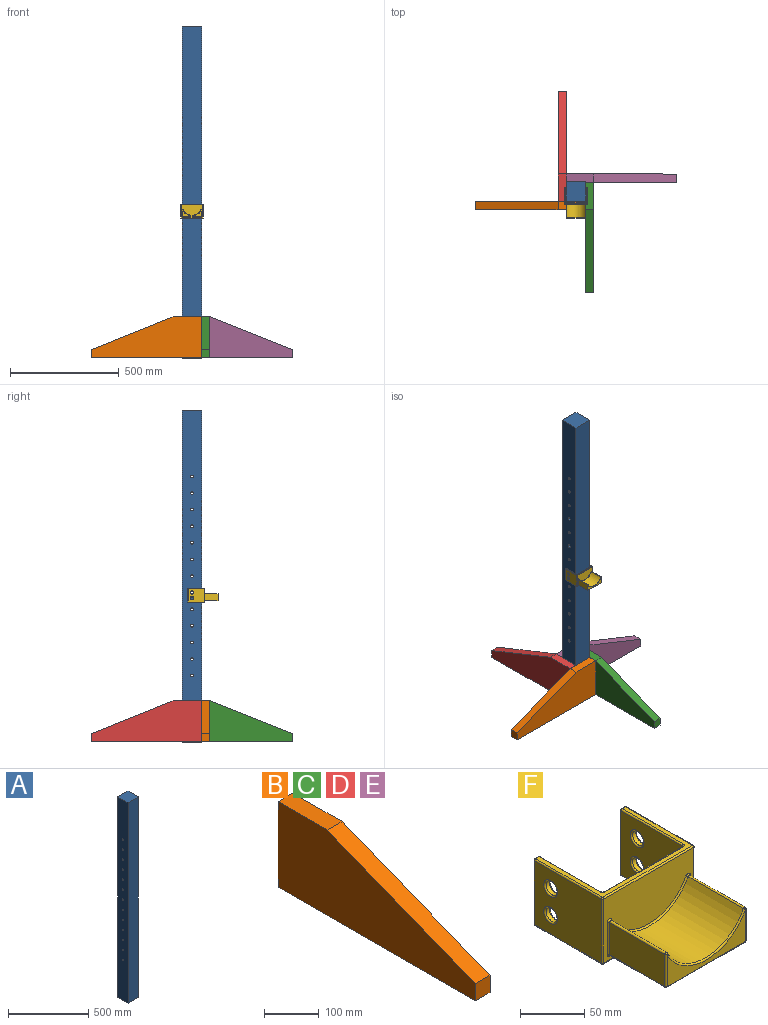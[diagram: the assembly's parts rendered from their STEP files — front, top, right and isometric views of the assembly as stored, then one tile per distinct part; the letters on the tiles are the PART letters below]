
ASSEMBLY  parts=6 mates=5
PART A: 19 faces, bbox 88.9x88.9x1524 mm
  f0: plane 1524x88.9mm, normal (0,1,0), area 135483.6mm2, adj f1,f3,f4,f5
  f1: plane 1524x88.9mm, normal (-1,0,0), area 133836.8mm2, adj f0,f2,f4,f5,f6,f7,f8,f9
  f2: plane 1524x88.9mm, normal (0,-1,0), area 135483.6mm2, adj f1,f3,f4,f5
  f3: plane 1524x88.9mm, normal (1,0,0), area 133836.8mm2, adj f0,f2,f4,f5,f6,f7,f8,f9
  f4: plane 88.9x88.9mm, normal (0,0,1), area 7903.2mm2, adj f0,f1,f2,f3
  f5: plane 88.9x88.9mm, normal (0,0,-1), area 7903.2mm2, adj f0,f1,f2,f3
  f6: cylinder r=6.35mm len=88.9mm, axis (1,0,0), area 3547mm2, adj f1,f3
  f7: cylinder r=6.35mm len=88.9mm, axis (1,0,0), area 3547mm2, adj f1,f3
  f8: cylinder r=6.35mm len=88.9mm, axis (1,0,0), area 3547mm2, adj f1,f3
  f9: cylinder r=6.35mm len=88.9mm, axis (1,0,0), area 3547mm2, adj f1,f3
  f10: cylinder r=6.35mm len=88.9mm, axis (1,0,0), area 3547mm2, adj f1,f3
  f11: cylinder r=6.35mm len=88.9mm, axis (1,0,0), area 3547mm2, adj f1,f3
  f12: cylinder r=6.35mm len=88.9mm, axis (1,0,0), area 3547mm2, adj f1,f3
  f13: cylinder r=6.35mm len=88.9mm, axis (1,0,0), area 3547mm2, adj f1,f3
  f14: cylinder r=6.35mm len=88.9mm, axis (1,0,0), area 3547mm2, adj f1,f3
  f15: cylinder r=6.35mm len=88.9mm, axis (1,0,0), area 3547mm2, adj f1,f3
  f16: cylinder r=6.35mm len=88.9mm, axis (1,0,0), area 3547mm2, adj f1,f3
  f17: cylinder r=6.35mm len=88.9mm, axis (1,0,0), area 3547mm2, adj f1,f3
  f18: cylinder r=6.35mm len=88.9mm, axis (1,0,0), area 3547mm2, adj f1,f3
PART B: 7 faces, bbox 38.1x508x190.5 mm
  f0: plane 127x38.1mm, normal (0,0,1), area 4838.7mm2, adj f1,f4,f5,f6
  f1: plane 381x152.4mm, normal (0,-0.37,0.93), area 15634.3mm2, adj f0,f2,f5,f6
  f2: plane 38.1x38.1mm, normal (0,-1,0), area 1451.6mm2, adj f1,f3,f5,f6
  f3: plane 508x38.1mm, normal (0,0,-1), area 19354.8mm2, adj f2,f4,f5,f6
  f4: plane 190.5x38.1mm, normal (0,1,0), area 7258.1mm2, adj f0,f3,f5,f6
  f5: plane 508x190.5mm, normal (1,0,0), area 67741.8mm2, adj f0,f1,f2,f3,f4
  f6: plane 508x190.5mm, normal (-1,0,0), area 67741.8mm2, adj f0,f1,f2,f3,f4
PART C: same geometry as B
PART D: same geometry as B
PART E: same geometry as B
PART F: 87 faces, bbox 101.6x139.7x63.5 mm
  f0: plane 99.06x73.66mm, normal (0,0,-1), area 912.4mm2, adj f35,f39,f40,f44,f49,f50,f54,f59
  f1: plane 99.06x73.66mm, normal (0,0,1), area 912.4mm2, adj f42,f47,f52,f53,f57,f63,f64,f68
  f2: plane 60.96x3.81mm, normal (0,1,0), area 232.3mm2, adj f35,f38,f41,f42
  f3: plane 73.66x60.96mm, normal (-1,0,0), area 4125.5mm2, adj f40,f41,f51,f52,f85,f86
  f4: plane 99.06x60.96mm, normal (0,-1,0), area 4386.5mm2, adj f20,f25,f26,f29,f30,f32,f33,f34
  f5: plane 73.66x60.96mm, normal (1,0,0), area 4125.5mm2, adj f61,f62,f70,f71,f79,f82
  f6: plane 60.96x3.81mm, normal (0,1,0), area 232.3mm2, adj f60,f69,f70,f74
  f7: plane 67.31x60.96mm, normal (1,0,0), area 3738.4mm2, adj f38,f39,f47,f48,f80,f83
  f8: plane 86.36x60.96mm, normal (0,1,0), area 5264.5mm2, adj f48,f49,f57,f58
  f9: plane 67.31x60.96mm, normal (-1,0,0), area 3738.4mm2, adj f58,f59,f68,f69,f81,f84
  f10: cylinder r=46.99mm len=84.09mm, axis (0,1,0), area 6346.8mm2, adj f23,f28,f31,f34
  f11: plane 60.96x30.52mm, normal (-1,0,0), area 1860.3mm2, adj f18,f19,f28,f29
  f12: plane 86.36x60.96mm, normal (0,0,-1), area 5264.5mm2, adj f15,f19,f20,f21
  f13: plane 60.96x30.52mm, normal (1,0,0), area 1860.3mm2, adj f21,f22,f30,f31
  f14: plane 86.36x30.52mm, normal (0,-1,0), area 985.9mm2, adj f15,f18,f22,f23
  f15: cylinder r=1.27mm len=86.36mm, axis (-1,0,0), area 172.3mm2, adj f12,f14,f16,f17
  f16: sphere r=1.27mm, area 2.5mm2, adj f15,f18,f19
  f17: sphere r=1.27mm, area 2.5mm2, adj f15,f21,f22
  f18: cylinder r=1.27mm len=30.52mm, axis (0,0,1), area 60.9mm2, adj f11,f14,f16,f24
  f19: cylinder r=1.27mm len=60.96mm, axis (0,1,0), area 121.6mm2, adj f11,f12,f16,f25
  f20: cylinder r=1.27mm len=86.36mm, axis (-1,0,0), area 172.3mm2, adj f4,f12,f25,f26
  f21: cylinder r=1.27mm len=60.96mm, axis (0,-1,0), area 121.6mm2, adj f12,f13,f17,f26
  f22: cylinder r=1.27mm len=30.52mm, axis (0,0,-1), area 60.9mm2, adj f13,f14,f17,f27
  f23: torus R=48.26mm, axis (0,-1,0), area 209.7mm2, adj f10,f14,f24,f27
  f24: sphere r=1.27mm, area 4.3mm2, adj f18,f23,f28
  f25: torus R=2.54mm, axis (0,1,0), area 5.4mm2, adj f4,f19,f20,f29
  f26: torus R=2.54mm, axis (0,1,0), area 5.4mm2, adj f4,f20,f21,f30
  f27: sphere r=1.27mm, area 4.3mm2, adj f22,f23,f31
  f28: cylinder r=1.27mm len=60.96mm, axis (0,1,0), area 207.4mm2, adj f10,f11,f24,f32
  f29: cylinder r=1.27mm len=30.52mm, axis (0,0,1), area 60.9mm2, adj f4,f11,f25,f32
  f30: cylinder r=1.27mm len=30.52mm, axis (0,0,-1), area 60.9mm2, adj f4,f13,f26,f33
  f31: cylinder r=1.27mm len=60.96mm, axis (0,1,0), area 207.4mm2, adj f10,f13,f27,f33
  f32: torus R=2.54mm, axis (0,1,0), area 9.3mm2, adj f4,f28,f29,f34
  f33: torus R=2.54mm, axis (0,1,0), area 9.3mm2, adj f4,f30,f31,f34
  f34: torus R=45.72mm, axis (0,1,0), area 205.7mm2, adj f4,f10,f32,f33
  f35: cylinder r=1.27mm len=3.81mm, axis (-1,0,0), area 7.6mm2, adj f0,f2,f36,f37
  f36: sphere r=1.27mm, area 2.5mm2, adj f35,f38,f39
  f37: sphere r=1.27mm, area 2.5mm2, adj f35,f40,f41
  f38: cylinder r=1.27mm len=60.96mm, axis (0,0,1), area 121.6mm2, adj f2,f7,f36,f43
  f39: cylinder r=1.27mm len=67.31mm, axis (0,1,0), area 134.3mm2, adj f0,f7,f36,f44
  f40: cylinder r=1.27mm len=73.66mm, axis (0,-1,0), area 146.9mm2, adj f0,f3,f37,f45
  f41: cylinder r=1.27mm len=60.96mm, axis (0,0,-1), area 121.6mm2, adj f2,f3,f37,f46
  f42: cylinder r=1.27mm len=3.81mm, axis (1,0,0), area 7.6mm2, adj f1,f2,f43,f46
  f43: sphere r=1.27mm, area 2.5mm2, adj f38,f42,f47
  f44: torus R=2.54mm, axis (0,0,1), area 5.4mm2, adj f0,f39,f48,f49
  f45: sphere r=1.27mm, area 2.5mm2, adj f40,f50,f51
  f46: sphere r=1.27mm, area 2.5mm2, adj f41,f42,f52
  f47: cylinder r=1.27mm len=67.31mm, axis (0,-1,0), area 134.3mm2, adj f1,f7,f43,f53
  f48: cylinder r=1.27mm len=60.96mm, axis (0,0,-1), area 121.6mm2, adj f7,f8,f44,f53
  f49: cylinder r=1.27mm len=86.36mm, axis (-1,0,0), area 172.3mm2, adj f0,f8,f44,f54
  f50: cylinder r=1.27mm len=99.06mm, axis (1,0,0), area 197.6mm2, adj f0,f4,f45,f55
  f51: cylinder r=1.27mm len=60.96mm, axis (0,0,1), area 121.6mm2, adj f3,f4,f45,f56
  f52: cylinder r=1.27mm len=73.66mm, axis (0,1,0), area 146.9mm2, adj f1,f3,f46,f56
  f53: torus R=2.54mm, axis (0,0,1), area 5.4mm2, adj f1,f47,f48,f57
  f54: torus R=2.54mm, axis (0,0,1), area 5.4mm2, adj f0,f49,f58,f59
  f55: sphere r=1.27mm, area 2.5mm2, adj f50,f61,f62
  f56: sphere r=1.27mm, area 2.5mm2, adj f51,f52,f63
  f57: cylinder r=1.27mm len=86.36mm, axis (1,0,0), area 172.3mm2, adj f1,f8,f53,f64
  f58: cylinder r=1.27mm len=60.96mm, axis (0,0,1), area 121.6mm2, adj f8,f9,f54,f64
  f59: cylinder r=1.27mm len=67.31mm, axis (0,-1,0), area 134.3mm2, adj f0,f9,f54,f65
  f60: cylinder r=1.27mm len=3.81mm, axis (-1,0,0), area 7.6mm2, adj f0,f6,f65,f66
  f61: cylinder r=1.27mm len=73.66mm, axis (0,1,0), area 146.9mm2, adj f0,f5,f55,f66
  f62: cylinder r=1.27mm len=60.96mm, axis (0,0,-1), area 121.6mm2, adj f4,f5,f55,f67
  f63: cylinder r=1.27mm len=99.06mm, axis (-1,0,0), area 197.6mm2, adj f1,f4,f56,f67
  f64: torus R=2.54mm, axis (0,0,1), area 5.4mm2, adj f1,f57,f58,f68
  f65: sphere r=1.27mm, area 2.5mm2, adj f59,f60,f69
  f66: sphere r=1.27mm, area 2.5mm2, adj f60,f61,f70
  f67: sphere r=1.27mm, area 2.5mm2, adj f62,f63,f71
  f68: cylinder r=1.27mm len=67.31mm, axis (0,1,0), area 134.3mm2, adj f1,f9,f64,f72
  f69: cylinder r=1.27mm len=60.96mm, axis (0,0,-1), area 121.6mm2, adj f6,f9,f65,f72
  f70: cylinder r=1.27mm len=60.96mm, axis (0,0,1), area 121.6mm2, adj f5,f6,f66,f73
  f71: cylinder r=1.27mm len=73.66mm, axis (0,-1,0), area 146.9mm2, adj f1,f5,f67,f73
  f72: sphere r=1.27mm, area 2.5mm2, adj f68,f69,f74
  f73: sphere r=1.27mm, area 2.5mm2, adj f70,f71,f74
  f74: cylinder r=1.27mm len=3.81mm, axis (1,0,0), area 7.6mm2, adj f1,f6,f72,f73
  f75: cylinder r=6.35mm len=12.7mm, axis (-1,0,0), area 152mm2, adj f82,f84
  f76: cylinder r=6.35mm len=12.7mm, axis (-1,0,0), area 152mm2, adj f79,f81
  f77: cylinder r=6.35mm len=12.7mm, axis (-1,0,0), area 152mm2, adj f83,f85
  f78: cylinder r=6.35mm len=12.7mm, axis (-1,0,0), area 152mm2, adj f80,f86
  f79: torus R=7.62mm, axis (-1,0,0), area 85.4mm2, adj f5,f76
  f80: torus R=7.62mm, axis (-1,0,0), area 85.4mm2, adj f7,f78
  f81: torus R=7.62mm, axis (-1,0,0), area 85.4mm2, adj f9,f76
  f82: torus R=7.62mm, axis (-1,0,0), area 85.4mm2, adj f5,f75
  f83: torus R=7.62mm, axis (-1,0,0), area 85.4mm2, adj f7,f77
  f84: torus R=7.62mm, axis (-1,0,0), area 85.4mm2, adj f9,f75
  f85: torus R=7.62mm, axis (-1,0,0), area 85.4mm2, adj f3,f77
  f86: torus R=7.62mm, axis (-1,0,0), area 85.4mm2, adj f3,f78
PLACE A t=(-558.86,284.42,-21.93)mm fixed
PLACE B rot(axis=(0,0,-1),90deg) t=(-476.5,-62.6,300.67)mm
PLACE C t=(-117.26,-332.95,300.67)mm
PLACE D rot(axis=(0,0,-1),180deg) t=(-206.16,296.64,300.67)mm
PLACE E rot(axis=(0,0,1),90deg) t=(153.08,26.3,300.67)mm
PLACE F t=(-212.51,-75.3,619.42)mm
MATE fastened C.f6 <-> A.f3  axis (-1,0,0) through (-117.26,26.3,-21.93)mm
MATE fastened B.f6 <-> A.f2  axis (0,1,0) through (-117.26,-62.6,-21.93)mm
MATE fastened A.f13 <-> F.f76  axis (-1,0,0) through (-206.16,-18.15,663.87)mm
MATE fastened A.f0 <-> E.f6  axis (0,1,0) through (-206.16,26.3,-21.93)mm
MATE fastened A.f1 <-> D.f6  axis (-1,0,0) through (-206.16,-62.6,-21.93)mm
